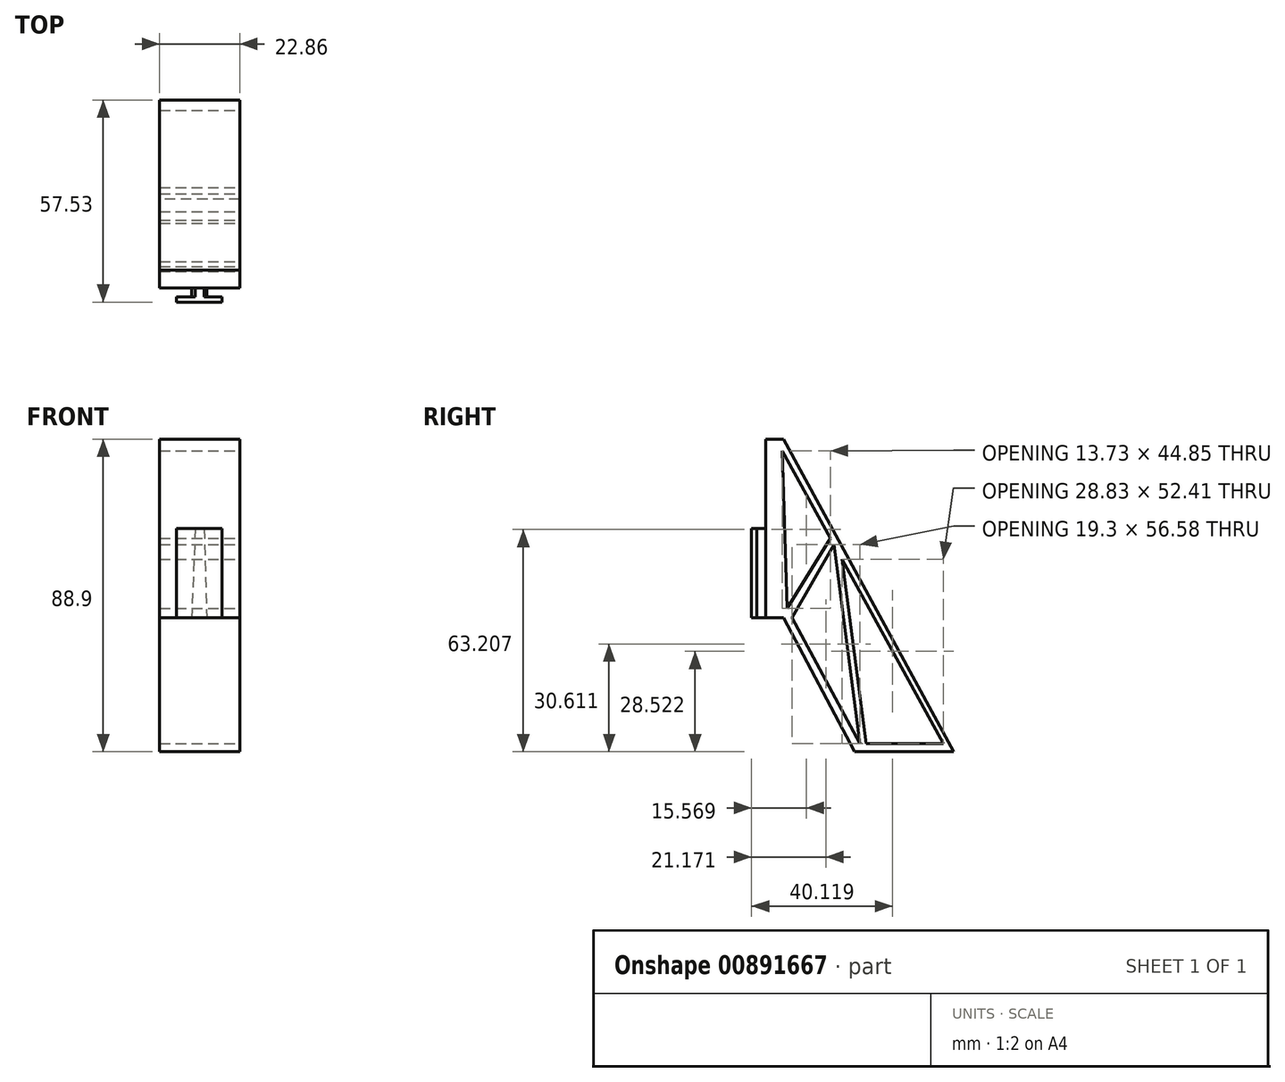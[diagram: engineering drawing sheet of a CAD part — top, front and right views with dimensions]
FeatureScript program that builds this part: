
annotation { "Feature Type Name" : "Feature", "Feature Type Description" : "" }
export const myFeature = defineFeature(function(context is Context, id is Id, definition is map)
    precondition{}
    {
        {
            var Q0;
            Q0=qCreatedBy(makeId("Front.planeOp"),FACE);
            var sketch = newSketch(context, id + "F0", { "sketchPlane" : qUnion([Q0])});
            skLineSegment(sketch, "E0.bottom", {"start": v(-11.43, 25.4) * mm, "end": v(11.43, 25.4) * mm});
            skLineSegment(sketch, "E0.top", {"start": v(-11.43, -25.4) * mm, "end": v(11.43, -25.4) * mm});
            skLineSegment(sketch, "E0.left", {"start": v(-11.43, 25.4) * mm, "end": v(-11.43, -25.4) * mm});
            skLineSegment(sketch, "E0.right", {"start": v(11.43, 25.4) * mm, "end": v(11.43, -25.4) * mm});
            skPoint(sketch, "E0.middle", {"position": v(0, 0) * mm});
            skLineSegment(sketch, "E1.bottom", {"start": v(-6.35, -25.4) * mm, "end": v(6.35, -25.4) * mm});
            skLineSegment(sketch, "E1.top", {"start": v(-6.35, 0) * mm, "end": v(6.35, 0) * mm});
            skLineSegment(sketch, "E1.left", {"start": v(-6.35, -25.4) * mm, "end": v(-6.35, 0) * mm});
            skLineSegment(sketch, "E1.right", {"start": v(6.35, -25.4) * mm, "end": v(6.35, 0) * mm});
            skLineSegment(sketch, "E2", {"start": v(-1.27, 0) * mm, "end": v(-2.29, -25.4) * mm});
            skLineSegment(sketch, "E3", {"start": v(1.27, 0) * mm, "end": v(2.03, -25.4) * mm});
            skSolve(sketch);
        }
        {
            var Q0;
            Q0=makeQuery(id+"F0.imprint","IMPRINT",FACE,{"disambiguationData":[TD([[makeQuery(id+"F0.imprint","IMPRINT",EDGE,{"derivedFrom":sQuery(id+"F0.wireOp",EDGE,"E0.bottom")}),-1.0]])]});
            var Q1;
            {var subQ0=sQuery(id+"F0.wireOp",EDGE,"E1.left");Q1=makeQuery(id+"F0.imprint","IMPRINT",FACE,{"disambiguationData":[TD([[makeQuery(id+"F0.imprint","IMPRINT",EDGE,{"derivedFrom":subQ0}),-1.0]])]});}
            var Q2;
            {var subQ0=sQuery(id+"F0.wireOp",EDGE,"E2");Q2=makeQuery(id+"F0.imprint","IMPRINT",FACE,{"disambiguationData":[TD([[makeQuery(id+"F0.imprint","IMPRINT",EDGE,{"derivedFrom":subQ0}),1.0]])]});}
            var Q3;
            {var subQ0=sQuery(id+"F0.wireOp",EDGE,"E1.right");Q3=makeQuery(id+"F0.imprint","IMPRINT",FACE,{"disambiguationData":[TD([[makeQuery(id+"F0.imprint","IMPRINT",EDGE,{"derivedFrom":subQ0}),1.0]])]});}
            extrude(context, id + "F1", {"entities" : qUnion([Q0, Q1, Q2, Q3]), "oppositeDirection" : true, "depth" : 5.08 * mm, "offsetDistance" : 25.4 * mm});
        }
        {
            var Q0;
            {var subQ0=sQuery(id+"F0.wireOp",EDGE,"E2");Q0=makeQuery(id+"F0.imprint","IMPRINT",FACE,{"disambiguationData":[TD([[makeQuery(id+"F0.imprint","IMPRINT",EDGE,{"derivedFrom":subQ0}),1.0]])]});}
            extrude(context, id + "F2", {"entities" : qUnion([Q0]), "operationType" : NewBodyOperationType.ADD, "depth" : 2.54 * mm, "offsetDistance" : 25.4 * mm});
        }
        {
            var Q0;
            Q0=makeQuery(id+"F2.opExtrude","CAP_FACE",FACE,{"disambiguationData":[OSD([sQuery(id+"F0.wireOp",EDGE,"E1.bottom"),sQuery(id+"F0.wireOp",EDGE,"E1.top"),sQuery(id+"F0.wireOp",EDGE,"E2"),sQuery(id+"F0.wireOp",EDGE,"E3")])],"isStart":false});
            var sketch = newSketch(context, id + "F3", { "sketchPlane" : qUnion([Q0])});
            skLineSegment(sketch, "E4.bottom", {"start": v(-6.57, 0) * mm, "end": v(6.31, 0) * mm});
            skLineSegment(sketch, "E4.top", {"start": v(-6.57, -25.4) * mm, "end": v(6.31, -25.4) * mm});
            skLineSegment(sketch, "E4.left", {"start": v(-6.57, 0) * mm, "end": v(-6.57, -25.4) * mm});
            skLineSegment(sketch, "E4.right", {"start": v(6.31, 0) * mm, "end": v(6.31, -25.4) * mm});
            skPoint(sketch, "E4.middle", {"position": v(-0.13, -12.7) * mm});
            skPoint(sketch, "E4.middle.positionSnap0", {"position": v(-1.78, -12.7) * mm});
            skPoint(sketch, "E4.middle.positionSnap1", {"position": v(-0.13, -25.4) * mm});
            skPoint(sketch, "E4.centerSnap0", {"position": v(-1.78, -12.7) * mm});
            skPoint(sketch, "E4.centerSnap1", {"position": v(-0.13, -25.4) * mm});
            skSolve(sketch);
        }
        {
            var Q0;
            {var subQ2=sQuery(id+"F3.wireOp",EDGE,"E4.right");Q0=makeQuery(id+"F3.imprint","IMPRINT",FACE,{"disambiguationData":[TD([[makeQuery(id+"F3.imprint","IMPRINT",EDGE,{"derivedFrom":subQ2}),-1.0]])]});}
            var Q1;
            {var subQ1=makeQuery(id+"F2.opExtrude","CAP_EDGE",EDGE,{"disambiguationData":[OSD([sQuery(id+"F0.wireOp",EDGE,"E2")])],"isStart":false});Q1=makeQuery(id+"F3.imprint","IMPRINT",FACE,{"disambiguationData":[TD([[makeQuery(id+"F3.imprint","IMPRINT",EDGE,{"derivedFrom":subQ1}),1.0]])]});}
            var Q2;
            {var subQ2=sQuery(id+"F3.wireOp",EDGE,"E4.left");Q2=makeQuery(id+"F3.imprint","IMPRINT",FACE,{"disambiguationData":[TD([[makeQuery(id+"F3.imprint","IMPRINT",EDGE,{"derivedFrom":subQ2}),1.0]])]});}
            extrude(context, id + "F4", {"entities" : qUnion([Q0, Q1, Q2]), "operationType" : NewBodyOperationType.ADD, "depth" : 1.52 * mm, "offsetDistance" : 25.4 * mm});
        }
        {
            var Q0;
            Q0=makeQuery(id+"F1.opExtrude","SWEPT_FACE",FACE,{"disambiguationData":[OSD([sQuery(id+"F0.wireOp",EDGE,"E0.left")])]});
            var sketch = newSketch(context, id + "F5", { "sketchPlane" : qUnion([Q0])});
            skLineSegment(sketch, "E5", {"start": v(-5.08, 25.4) * mm, "end": v(-53.47, -63.5) * mm});
            skLineSegment(sketch, "E6", {"start": v(-53.47, -63.5) * mm, "end": v(-25.28, -63.5) * mm});
            skLineSegment(sketch, "E7", {"start": v(-25.28, -63.5) * mm, "end": v(-5.08, -25.4) * mm});
            skLineSegment(sketch, "E8", {"start": v(-5.08, -25.4) * mm, "end": v(-5.08, 25.4) * mm});
            skSolve(sketch);
        }
        {
            var Q0;
            Q0=makeQuery(id+"F5.imprint","IMPRINT",FACE,{"disambiguationData":[TD([[makeQuery(id+"F5.imprint","IMPRINT",EDGE,{"derivedFrom":sQuery(id+"F5.wireOp",EDGE,"E5")}),1.0]])]});
            var Q1;
            Q1=makeQuery(id+"F1.opExtrude","SWEPT_FACE",FACE,{"disambiguationData":[OSD([sQuery(id+"F0.wireOp",EDGE,"E0.right")])]});
            extrude(context, id + "F6", {"entities" : qUnion([Q0]), "operationType" : NewBodyOperationType.ADD, "endBound" : BoundingType.UP_TO_SURFACE, "oppositeDirection" : true, "depth" : 25.4 * mm, "endBoundEntityFace" : qUnion([Q1]), "offsetDistance" : 25.4 * mm});
        }
        {
            var Q0;
            Q0=makeQuery(id+"F6.boolean.opBoolean","MERGE",FACE,{"derivedFrom":[makeQuery(id+"F1.opExtrude","SWEPT_FACE",FACE,{"disambiguationData":[OSD([sQuery(id+"F0.wireOp",EDGE,"E0.right")])]}),makeQuery(id+"F6.opExtrude","CAP_FACE",FACE,{"disambiguationData":[OSD([sQuery(id+"F5.wireOp",EDGE,"E5"),sQuery(id+"F5.wireOp",EDGE,"E6"),sQuery(id+"F5.wireOp",EDGE,"E7"),sQuery(id+"F5.wireOp",EDGE,"E8")])],"isStart":false})]});
            var sketch = newSketch(context, id + "F7", { "sketchPlane" : qUnion([Q0])});
            skLineSegment(sketch, "E9", {"start": v(4.65, 22.13) * mm, "end": v(18.37, -2.82) * mm});
            skLineSegment(sketch, "E10", {"start": v(50.47, -61.18) * mm, "end": v(28.51, -61.18) * mm});
            skLineSegment(sketch, "E11", {"start": v(26.76, -61.18) * mm, "end": v(7.46, -25.4) * mm});
            skLineSegment(sketch, "E12", {"start": v(6.01, -22.72) * mm, "end": v(4.65, 22.13) * mm});
            skLineSegment(sketch, "E13", {"start": v(6.01, -22.72) * mm, "end": v(18.37, -2.82) * mm});
            skLineSegment(sketch, "E14", {"start": v(19.35, -4.6) * mm, "end": v(7.46, -25.4) * mm});
            skLineSegment(sketch, "E15", {"start": v(7.46, -25.4) * mm, "end": v(26.76, -61.18) * mm});
            skLineSegment(sketch, "E16", {"start": v(19.35, -4.6) * mm, "end": v(26.76, -61.18) * mm});
            skLineSegment(sketch, "E17", {"start": v(28.51, -61.18) * mm, "end": v(21.65, -8.77) * mm});
            skLineSegment(sketch, "E18.trimOffspring", {"start": v(21.65, -8.77) * mm, "end": v(50.47, -61.18) * mm});
            skSolve(sketch);
        }
        {
            var Q0;
            Q0=makeQuery(id+"F7.imprint","IMPRINT",FACE,{"disambiguationData":[TD([[makeQuery(id+"F7.imprint","IMPRINT",EDGE,{"derivedFrom":sQuery(id+"F7.wireOp",EDGE,"E9")}),-1.0]])]});
            var Q1;
            Q1=makeQuery(id+"F7.imprint","IMPRINT",FACE,{"disambiguationData":[TD([[makeQuery(id+"F7.imprint","IMPRINT",EDGE,{"derivedFrom":sQuery(id+"F7.wireOp",EDGE,"E14")}),1.0]])]});
            var Q2;
            Q2=makeQuery(id+"F7.imprint","IMPRINT",FACE,{"disambiguationData":[TD([[makeQuery(id+"F7.imprint","IMPRINT",EDGE,{"derivedFrom":sQuery(id+"F7.wireOp",EDGE,"E10")}),-1.0]])]});
            extrude(context, id + "F8", {"entities" : qUnion([Q0, Q1, Q2]), "operationType" : NewBodyOperationType.REMOVE, "oppositeDirection" : true, "depth" : 25.4 * mm, "offsetDistance" : 25.4 * mm});
        }
    });
